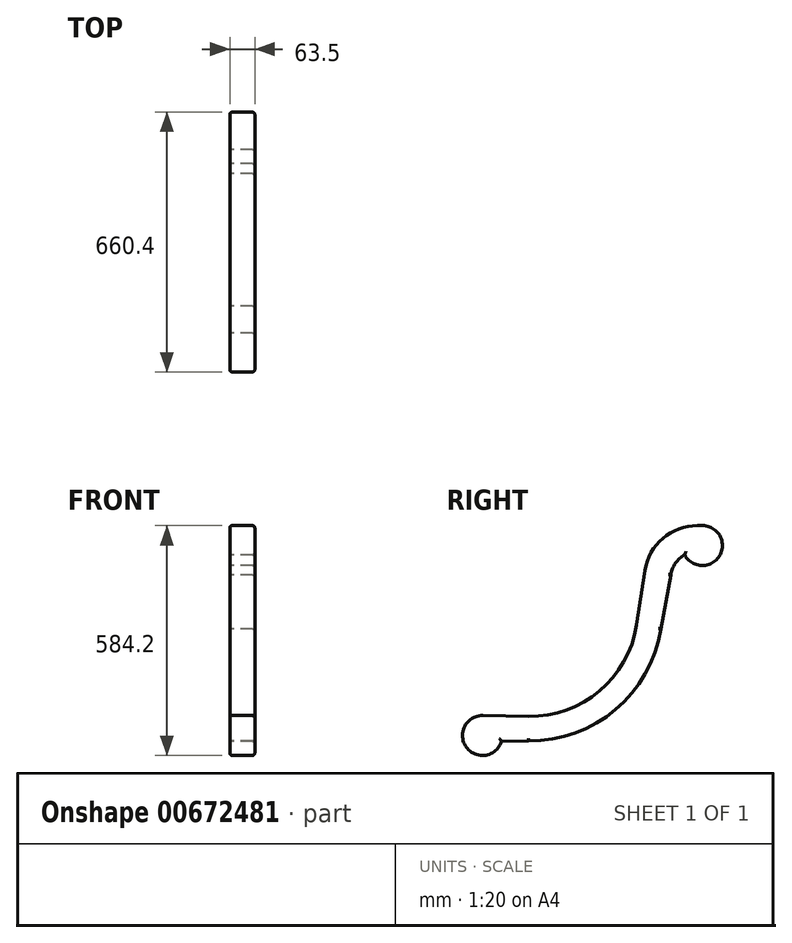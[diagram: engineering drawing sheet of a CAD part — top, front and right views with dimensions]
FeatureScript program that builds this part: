
annotation { "Feature Type Name" : "Feature", "Feature Type Description" : "" }
export const myFeature = defineFeature(function(context is Context, id is Id, definition is map)
    precondition{}
    {
        {
            var Q0;
            Q0=qCreatedBy(makeId("Right.planeOp"),FACE);
            var sketch = newSketch(context, id + "F0", { "sketchPlane" : qUnion([Q0])});
            skLineSegment(sketch, "E0.trimOffspring", {"start": v(-279.4, 533.4) * mm, "end": v(-279.4, 635) * mm, "construction": true});
            skLineSegment(sketch, "E1", {"start": v(0, 0) * mm, "end": v(0, 1066.8) * mm, "construction": true});
            skLineSegment(sketch, "E2.trimOffspring", {"start": v(279.4, 533.4) * mm, "end": v(279.4, 1117.6) * mm, "construction": true});
            skLineSegment(sketch, "E3", {"start": v(177.8, 406.4) * mm, "end": v(0, 406.4) * mm, "construction": true});
            skLineSegment(sketch, "E4.MirrorCS", {"start": v(-228.6, 406.4) * mm, "end": v(0, 406.4) * mm, "construction": true});
            skLineSegment(sketch, "E5", {"start": v(-279.4, 635) * mm, "end": v(-158.34, 635) * mm, "construction": true});
            skPoint(sketch, "E6.orphan", {"position": v(279.4, 1117.6) * mm});
            skLineSegment(sketch, "E7", {"start": v(279.4, 1117.6) * mm, "end": v(266.7, 1117.6) * mm, "construction": true});
            skLineSegment(sketch, "E8", {"start": v(166.52, 1032.93) * mm, "end": v(142.2, 889) * mm, "construction": true});
            skArc(sketch, "E9.filletArc", {"start": v(-158.34, 635) * mm, "mid": v(38.4, 707) * mm, "end": v(142.2, 889) * mm, "construction": true});
            skPoint(sketch, "E10.visualSharp", {"position": v(180.83, 1117.6) * mm});
            skArc(sketch, "E10.filletArc", {"start": v(266.7, 1117.6) * mm, "mid": v(201.12, 1093.6) * mm, "end": v(166.52, 1032.93) * mm, "construction": true});
            skLineSegment(sketch, "E11", {"start": v(177.8, 406.4) * mm, "end": v(241.3, 1012.68) * mm, "construction": true});
            skLineSegment(sketch, "E12", {"start": v(-279.4, 635) * mm, "end": v(186.38, 1079.78) * mm, "construction": true});
            skLineSegment(sketch, "E13", {"start": v(-379.2, 592.39) * mm, "end": v(282.12, 1223.89) * mm, "construction": true});
            skLineSegment(sketch, "E14", {"start": v(282.12, 1223.89) * mm, "end": v(448.77, 1049.38) * mm, "construction": true});
            skLineSegment(sketch, "E15", {"start": v(448.77, 1049.38) * mm, "end": v(-212.55, 417.87) * mm, "construction": true});
            skLineSegment(sketch, "E16", {"start": v(-212.55, 417.87) * mm, "end": v(-379.2, 592.39) * mm, "construction": true});
            skArc(sketch, "E17", {"start": v(-278.55, 668.23) * mm, "mid": v(-320.5, 587.57) * mm, "end": v(-230.83, 602.56) * mm});
            skArc(sketch, "E18", {"start": v(234.47, 1076.33) * mm, "mid": v(322.9, 1073.8) * mm, "end": v(279.4, 1150.84) * mm});
            skLineSegment(sketch, "E19", {"start": v(-278.55, 668.23) * mm, "end": v(-162.9, 666.3) * mm});
            skArc(sketch, "E20", {"start": v(-162.9, 666.3) * mm, "mid": v(17.92, 730.63) * mm, "end": v(111.97, 897.94) * mm});
            skLineSegment(sketch, "E21", {"start": v(279.4, 1150.84) * mm, "end": v(266.7, 1150.84) * mm});
            skLineSegment(sketch, "E22", {"start": v(133.45, 1036.64) * mm, "end": v(111.97, 897.94) * mm});
            skLineSegment(sketch, "E23.MirrorCS", {"start": v(-230.83, 602.56) * mm, "end": v(-162.9, 603.7) * mm});
            skLineSegment(sketch, "E24.MirrorCS", {"start": v(198.97, 1025.56) * mm, "end": v(173.67, 887.5) * mm});
            skArc(sketch, "E25", {"start": v(234.47, 1076.33) * mm, "mid": v(210.65, 1055.2) * mm, "end": v(198.97, 1025.56) * mm});
            skArc(sketch, "E26.trimOffspring", {"start": v(266.7, 1150.84) * mm, "mid": v(175.79, 1115.58) * mm, "end": v(132.42, 1028.25) * mm});
            skPoint(sketch, "E27.orphan", {"position": v(-278.55, 601.77) * mm});
            skArc(sketch, "E28", {"start": v(-322.53, 646.5) * mm, "mid": v(-322, 646.2) * mm, "end": v(-321.48, 645.9) * mm});
            skArc(sketch, "E29.trimOffspring", {"start": v(-162.9, 603.7) * mm, "mid": v(58.64, 683.09) * mm, "end": v(173.82, 888.33) * mm});
            skSolve(sketch);
        }
        {
            var Q0;
            Q0=makeQuery(id+"F0.imprint","IMPRINT",FACE,{"disambiguationData":[TD([[makeQuery(id+"F0.imprint","IMPRINT",EDGE,{"derivedFrom":sQuery(id+"F0.wireOp",EDGE,"E18")}),1.0]])]});
            extrude(context, id + "F1", {"entities" : qUnion([Q0]), "depth" : 38.1 * mm, "offsetDistance" : 25.4 * mm, "hasSecondDirection" : true, "secondDirectionOppositeDirection" : true, "secondDirectionDepth" : 25.4 * mm});
        }
        {
            var Q0;
            Q0=makeQuery(id+"F1.opExtrude","CAP_FACE",FACE,{"disambiguationData":[OSD([sQuery(id+"F0.wireOp",EDGE,"E17"),sQuery(id+"F0.wireOp",EDGE,"E18"),sQuery(id+"F0.wireOp",EDGE,"E19"),sQuery(id+"F0.wireOp",EDGE,"E20"),sQuery(id+"F0.wireOp",EDGE,"E21"),sQuery(id+"F0.wireOp",EDGE,"E22"),sQuery(id+"F0.wireOp",EDGE,"E23.MirrorCS"),sQuery(id+"F0.wireOp",EDGE,"E24.MirrorCS"),sQuery(id+"F0.wireOp",EDGE,"E25"),sQuery(id+"F0.wireOp",EDGE,"E26.trimOffspring"),sQuery(id+"F0.wireOp",EDGE,"E29.trimOffspring")])],"isStart":false});
            var Q1;
            Q1=makeQuery(id+"F1.opExtrude","CAP_FACE",FACE,{"disambiguationData":[OSD([sQuery(id+"F0.wireOp",EDGE,"E17"),sQuery(id+"F0.wireOp",EDGE,"E18"),sQuery(id+"F0.wireOp",EDGE,"E19"),sQuery(id+"F0.wireOp",EDGE,"E20"),sQuery(id+"F0.wireOp",EDGE,"E21"),sQuery(id+"F0.wireOp",EDGE,"E22"),sQuery(id+"F0.wireOp",EDGE,"E23.MirrorCS"),sQuery(id+"F0.wireOp",EDGE,"E24.MirrorCS"),sQuery(id+"F0.wireOp",EDGE,"E25"),sQuery(id+"F0.wireOp",EDGE,"E26.trimOffspring"),sQuery(id+"F0.wireOp",EDGE,"E29.trimOffspring")])],"isStart":true});
            fillet(context, id + "F2", {"entities" : qUnion([Q0, Q1]), "radius" : 6.35 * mm, "tangentPropagation" : true, "allowEdgeOverflow" : false});
        }
    });
